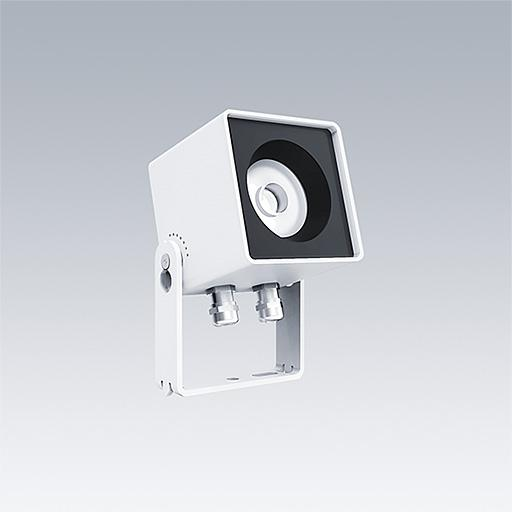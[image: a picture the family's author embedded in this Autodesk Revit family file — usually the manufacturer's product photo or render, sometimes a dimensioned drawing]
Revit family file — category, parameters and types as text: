
# Revit family: Thorn Caelon S7x
name_source: partatom
category: Lighting Fixtures
units: mm (PartAtom-declared; Revit-internal decimal feet)

## family parameters
Cut with Voids When Loaded = No
Host = Face
Light Source = No
Maintain Annotation Orientation = No
Part Type = Normal
Room Calculation Point = No
Round Connector Dimension = Use Diameter
Shared = No

## types (24) — shared parameters
Apparent Load = 20 VA
Assembly Code = Pr_70_70_48_75
Description = Outdoor flood and spotlight luminaires
Export Type to IFC As = IfcLightFixtureType
Lamp = LED
Luminaire Height = 127.02 mm  [stored 0.416732 ft]
Luminaire Length = 75 mm  [stored 0.246063 ft]
Luminaire Width = 86 mm  [stored 0.282152 ft]
Manufacturer = Thorn Lighting
Power Factor = 1
Type Bracket Black = Thorn-Parts-CAELON-Bracket-S7x : Black
Type Bracket White = Thorn-Parts-CAELON-Bracket-S7x : White
Type Housing Black = Thorn-Parts-CAELON-Housing-S7x : Black
Type Housing White = Thorn-Parts-CAELON-Housing-S7x : White
Type IFC Predefined Type = DIRECTIONSOURCE
URL = https://www.thornlighting.com
Wattage = 11 VA
zero-valued in all types: Default Elevation

## per-type parameters (varying)
| type | Housing Finish Black | Housing Finish White | Model | Optic | Type Bracket | Type Housing | Type Image | Type Light Source |
| CAELON S7x 700-827 F BK STD 66 | Yes | No | 21013563 | Far | Thorn-Parts-CAELON-Bracket-S7x : Black | Thorn-Parts-CAELON-Housing-S7x : Black | TLG_CAEL_F_S7x_BK.jpg | Thorn-Light Sources-CAELON S7x : CAELON S7x 700-827 F BK STD 66_photometric_data |
| CAELON S7x 700-827 F WH STD 66 | No | Yes | 21013562 | Far | Thorn-Parts-CAELON-Bracket-S7x : White | Thorn-Parts-CAELON-Housing-S7x : White | TLG_CAEL_F_S7x_BK.jpg | Thorn-Light Sources-CAELON S7x : CAELON S7x 700-827 F WH STD 66_photometric_data |
| CAELON S7x 700-827 M BK STD 66 | Yes | No | 21013561 | Medium | Thorn-Parts-CAELON-Bracket-S7x : Black | Thorn-Parts-CAELON-Housing-S7x : Black | TLG_CAEL_F_S7x_BK.jpg | Thorn-Light Sources-CAELON S7x : CAELON S7x 700-827 M BK STD 66_photometric_data |
| CAELON S7x 700-827 M WH STD 66 | No | Yes | 21013560 | Medium | Thorn-Parts-CAELON-Bracket-S7x : White | Thorn-Parts-CAELON-Housing-S7x : White | TLG_CAEL_F_S7x_WH.jpg | Thorn-Light Sources-CAELON S7x : CAELON S7x 700-827 M WH STD 66_photometric_data |
| CAELON S7x 700-827 N BK STD 66 | Yes | No | 21013559 | Narrow | Thorn-Parts-CAELON-Bracket-S7x : Black | Thorn-Parts-CAELON-Housing-S7x : Black | TLG_CAEL_F_S7x_BK.jpg | Thorn-Light Sources-CAELON S7x : CAELON S7x 700-827 N BK STD 66_photometric_data |
| CAELON S7x 700-827 N WH STD 66 | No | Yes | 21013558 | Narrow | Thorn-Parts-CAELON-Bracket-S7x : White | Thorn-Parts-CAELON-Housing-S7x : White | TLG_CAEL_F_S7x_WH.jpg | Thorn-Light Sources-CAELON S7x : CAELON S7x 700-827 N WH STD 66_photometric_data |
| CAELON S7x 700-827 SN BK STD 66 | Yes | No | 21013557 | Super Narrow | Thorn-Parts-CAELON-Bracket-S7x : Black | Thorn-Parts-CAELON-Housing-S7x : Black | TLG_CAEL_F_S7x_BK.jpg | Thorn-Light Sources-CAELON S7x : CAELON S7x 700-827 SN BK STD 66_photometric_data |
| CAELON S7x 700-827 SN WH STD 66 | No | Yes | 21013556 | Super Narrow | Thorn-Parts-CAELON-Bracket-S7x : White | Thorn-Parts-CAELON-Housing-S7x : White | TLG_CAEL_F_S7x_WH.jpg | Thorn-Light Sources-CAELON S7x : CAELON S7x 700-827 SN WH STD 66_photometric_data |
| CAELON S7x 700-830 F BK STD 66 | Yes | No | 21013571 | Far | Thorn-Parts-CAELON-Bracket-S7x : Black | Thorn-Parts-CAELON-Housing-S7x : Black | TLG_CAEL_F_S7x_BK.jpg | Thorn-Light Sources-CAELON S7x : CAELON S7x 700-830 F BK STD 66_photometric_data |
| CAELON S7x 700-830 F WH STD 66 | No | Yes | 21013570 | Far | Thorn-Parts-CAELON-Bracket-S7x : White | Thorn-Parts-CAELON-Housing-S7x : White | TLG_CAEL_F_S7x_WH.jpg | Thorn-Light Sources-CAELON S7x : CAELON S7x 700-830 F WH STD 66_photometric_data |
| CAELON S7x 700-830 M BK STD 66 | Yes | No | 21013569 | Medium | Thorn-Parts-CAELON-Bracket-S7x : Black | Thorn-Parts-CAELON-Housing-S7x : Black | TLG_CAEL_F_S7x_BK.jpg | Thorn-Light Sources-CAELON S7x : CAELON S7x 700-830 M BK STD 66_photometric_data |
| CAELON S7x 700-830 M WH STD 66 | No | Yes | 21013568 | Medium | Thorn-Parts-CAELON-Bracket-S7x : White | Thorn-Parts-CAELON-Housing-S7x : White | TLG_CAEL_F_S7x_WH.jpg | Thorn-Light Sources-CAELON S7x : CAELON S7x 700-830 M WH STD 66_photometric_data |
| CAELON S7x 700-830 N BK STD 66 | Yes | No | 21013567 | Narrow | Thorn-Parts-CAELON-Bracket-S7x : Black | Thorn-Parts-CAELON-Housing-S7x : Black | TLG_CAEL_F_S7x_BK.jpg | Thorn-Light Sources-CAELON S7x : CAELON S7x 700-830 N BK STD 66_photometric_data |
| CAELON S7x 700-830 N WH STD 66 | No | Yes | 21013566 | Narrow | Thorn-Parts-CAELON-Bracket-S7x : White | Thorn-Parts-CAELON-Housing-S7x : White | TLG_CAEL_F_S7x_WH.jpg | Thorn-Light Sources-CAELON S7x : CAELON S7x 700-830 N WH STD 66_photometric_data |
| CAELON S7x 700-830 SN BK STD 66 | Yes | No | 21013565 | Super Narrow | Thorn-Parts-CAELON-Bracket-S7x : Black | Thorn-Parts-CAELON-Housing-S7x : Black | TLG_CAEL_F_S7x_BK.jpg | Thorn-Light Sources-CAELON S7x : CAELON S7x 700-830 SN BK STD 66_photometric_data |
| CAELON S7x 700-830 SN WH STD 66 | No | Yes | 21013564 | Super Narrow | Thorn-Parts-CAELON-Bracket-S7x : White | Thorn-Parts-CAELON-Housing-S7x : White | TLG_CAEL_F_S7x_WH.jpg | Thorn-Light Sources-CAELON S7x : CAELON S7x 700-830 SN WH STD 66_photometric_data |
| CAELON S7x 700-840 F BK STD 66 | Yes | No | 21013579 | Far | Thorn-Parts-CAELON-Bracket-S7x : Black | Thorn-Parts-CAELON-Housing-S7x : Black | TLG_CAEL_F_S7x_BK.jpg | Thorn-Light Sources-CAELON S7x : CAELON S7x 700-840 F BK STD 66_photometric_data |
| CAELON S7x 700-840 F WH STD 66 | No | Yes | 21013578 | Far | Thorn-Parts-CAELON-Bracket-S7x : White | Thorn-Parts-CAELON-Housing-S7x : White | TLG_CAEL_F_S7x_WH.jpg | Thorn-Light Sources-CAELON S7x : CAELON S7x 700-840 F WH STD 66_photometric_data |
| CAELON S7x 700-840 M BK STD 66 | Yes | No | 21013577 | Medium | Thorn-Parts-CAELON-Bracket-S7x : Black | Thorn-Parts-CAELON-Housing-S7x : Black | TLG_CAEL_F_S7x_BK.jpg | Thorn-Light Sources-CAELON S7x : CAELON S7x 700-840 M BK STD 66_photometric_data |
| CAELON S7x 700-840 M WH STD 66 | No | Yes | 21013576 | Medium | Thorn-Parts-CAELON-Bracket-S7x : White | Thorn-Parts-CAELON-Housing-S7x : White | TLG_CAEL_F_S7x_WH.jpg | Thorn-Light Sources-CAELON S7x : CAELON S7x 700-840 M WH STD 66_photometric_data |
| CAELON S7x 700-840 N BK STD 66 | Yes | No | 21013575 | Narrow | Thorn-Parts-CAELON-Bracket-S7x : Black | Thorn-Parts-CAELON-Housing-S7x : Black | TLG_CAEL_F_S7x_WH.jpg | Thorn-Light Sources-CAELON S7x : CAELON S7x 700-840 N BK STD 66_photometric_data |
| CAELON S7x 700-840 N WH STD 66 | No | Yes | 21013574 | Narrow | Thorn-Parts-CAELON-Bracket-S7x : White | Thorn-Parts-CAELON-Housing-S7x : White | TLG_CAEL_F_S7x_WH.jpg | Thorn-Light Sources-CAELON S7x : CAELON S7x 700-840 N WH STD 66_photometric_data |
| CAELON S7x 700-840 SN BK STD 66 | Yes | No | 21013573 | Super Narrow | Thorn-Parts-CAELON-Bracket-S7x : Black | Thorn-Parts-CAELON-Housing-S7x : Black | TLG_CAEL_F_S7x_BK.jpg | Thorn-Light Sources-CAELON S7x : CAELON S7x 700-840 SN BK STD 66_photometric_data |
| CAELON S7x 700-840 SN WH STD 66 | No | Yes | 21013572 | Super Narrow | Thorn-Parts-CAELON-Bracket-S7x : White | Thorn-Parts-CAELON-Housing-S7x : White | TLG_CAEL_F_S7x_WH.jpg | Thorn-Light Sources-CAELON S7x : CAELON S7x 700-840 SN WH STD 66_photometric_data |

note: [stored X ft] marks values corroborated as IEEE doubles in the binary element streams (Revit-internal decimal feet)

## geometry (parser evidence)
native form markers: Sweep x10
no freeform markers — native parametric forms only
